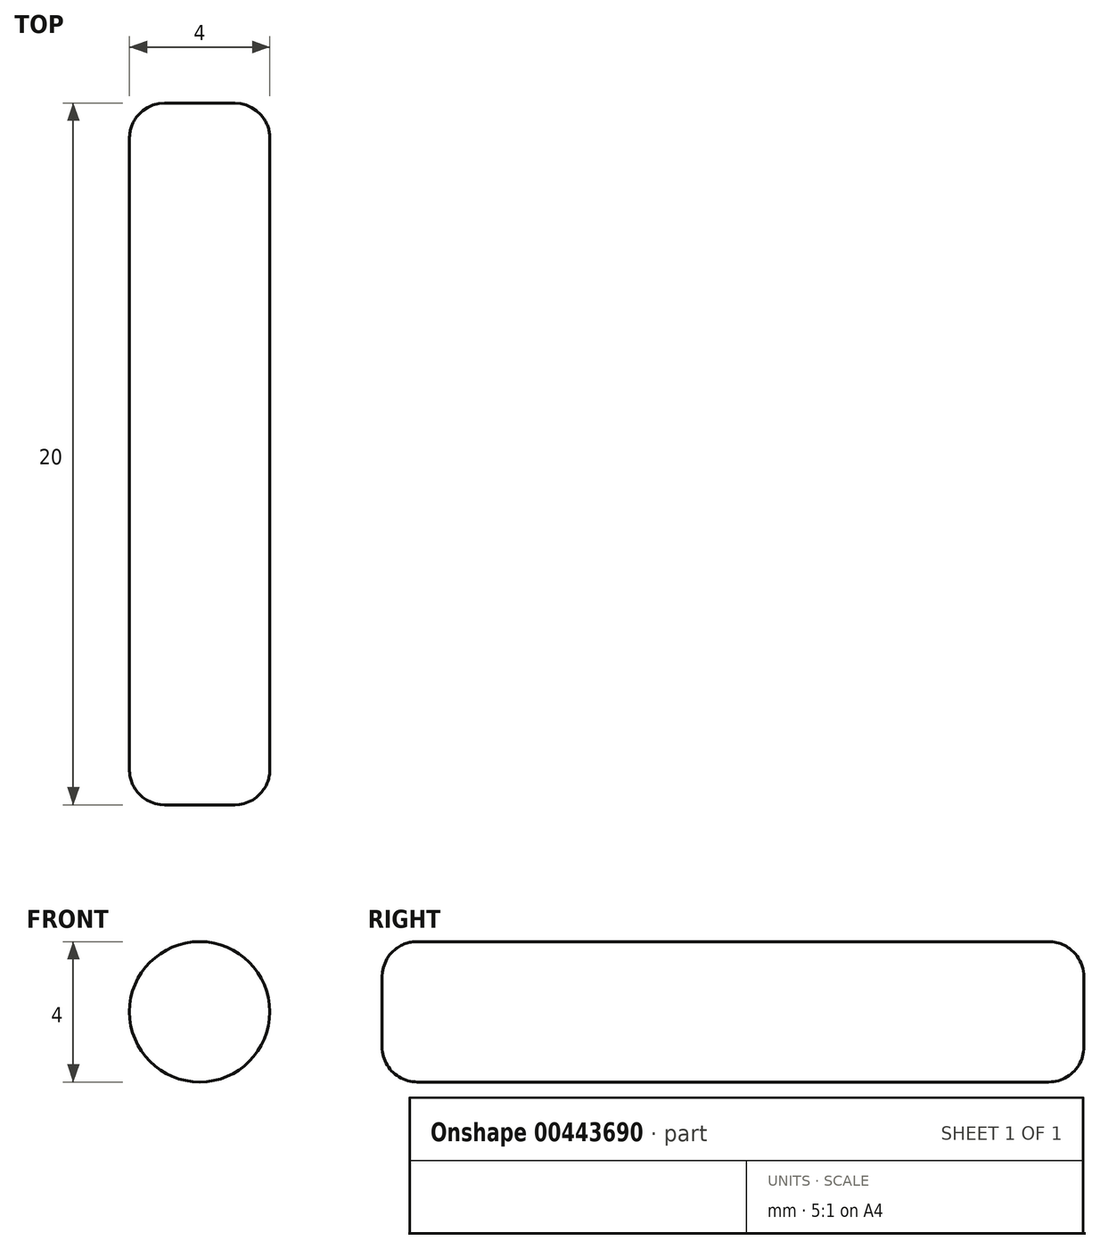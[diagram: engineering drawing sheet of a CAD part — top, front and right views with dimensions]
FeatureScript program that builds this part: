
annotation { "Feature Type Name" : "Feature", "Feature Type Description" : "" }
export const myFeature = defineFeature(function(context is Context, id is Id, definition is map)
    precondition{}
    {
        {
            var Q0;
            Q0=qCreatedBy(makeId("Front.planeOp"),FACE);
            var sketch = newSketch(context, id + "F0", { "sketchPlane" : qUnion([Q0])});
            skCircle(sketch, "E0", {"center": v(0, 0) * mm, "radius": 2 * mm});
            skSolve(sketch);
        }
        {
            var Q0;
            Q0 = qSketchRegion(id + "F0", true);
            extrude(context, id + "F1", {"entities" : qUnion([Q0]), "endBound" : BoundingType.SYMMETRIC, "depth" : 20 * mm});
        }
        {
            var Q0;
            Q0=makeQuery(id+"F1.opExtrude","CAP_FACE",FACE,{"disambiguationData":[OSD([sQuery(id+"F0.wireOp",EDGE,"E0")])],"isStart":false});
            var Q1;
            Q1=makeQuery(id+"F1.opExtrude","CAP_EDGE",EDGE,{"disambiguationData":[OSD([sQuery(id+"F0.wireOp",EDGE,"E0")])],"isStart":true});
            fillet(context, id + "F2", {"entities" : qUnion([Q0, Q1]), "radius" : 1 * mm, "tangentPropagation" : true, "allowEdgeOverflow" : false});
        }
    });
